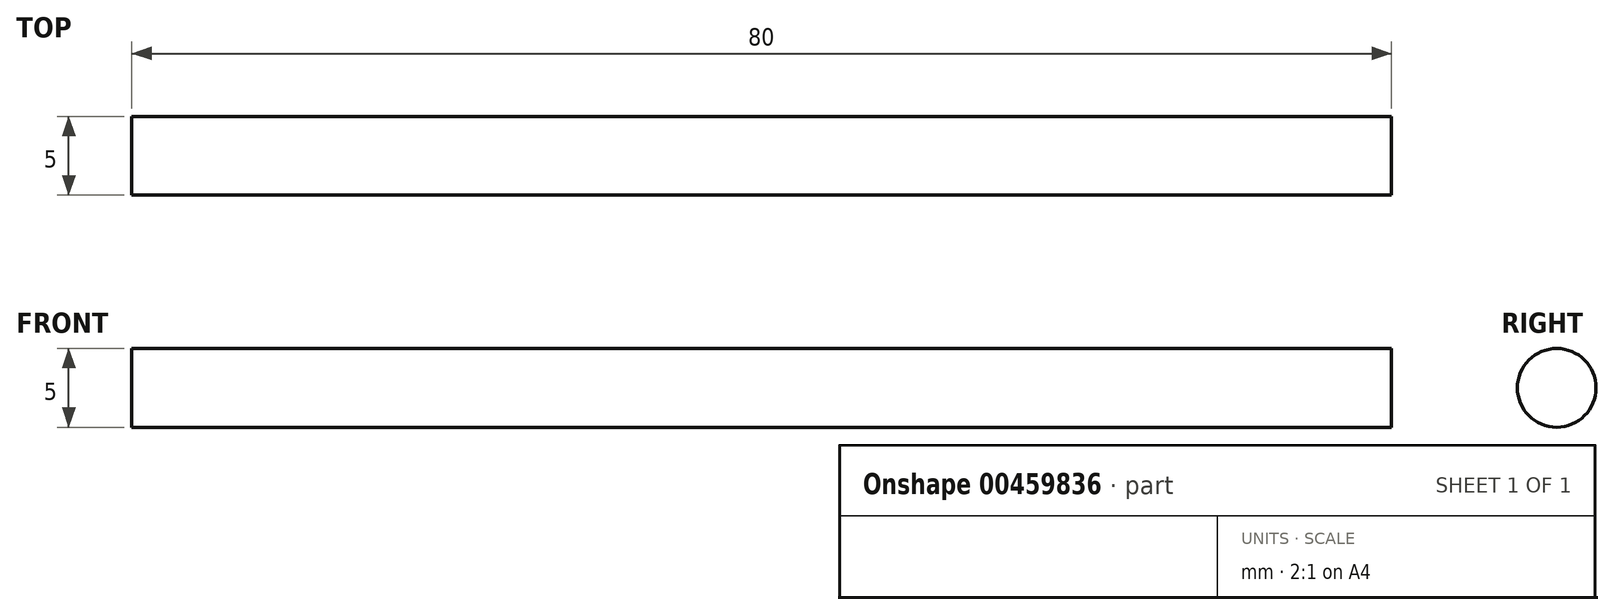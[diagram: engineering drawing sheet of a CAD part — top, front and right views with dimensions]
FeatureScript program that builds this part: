
annotation { "Feature Type Name" : "Feature", "Feature Type Description" : "" }
export const myFeature = defineFeature(function(context is Context, id is Id, definition is map)
    precondition{}
    {
        {
            var Q0;
            Q0=qCreatedBy(makeId("Right.planeOp"),FACE);
            var sketch = newSketch(context, id + "F0", { "sketchPlane" : qUnion([Q0])});
            skCircle(sketch, "E0", {"center": v(0, 0) * mm, "radius": 2.5 * mm});
            skSolve(sketch);
        }
        {
            var Q0;
            Q0 = qSketchRegion(id + "F0", true);
            extrude(context, id + "F1", {"entities" : qUnion([Q0]), "depth" : 80 * mm, "offsetDistance" : 25 * mm});
        }
    });
